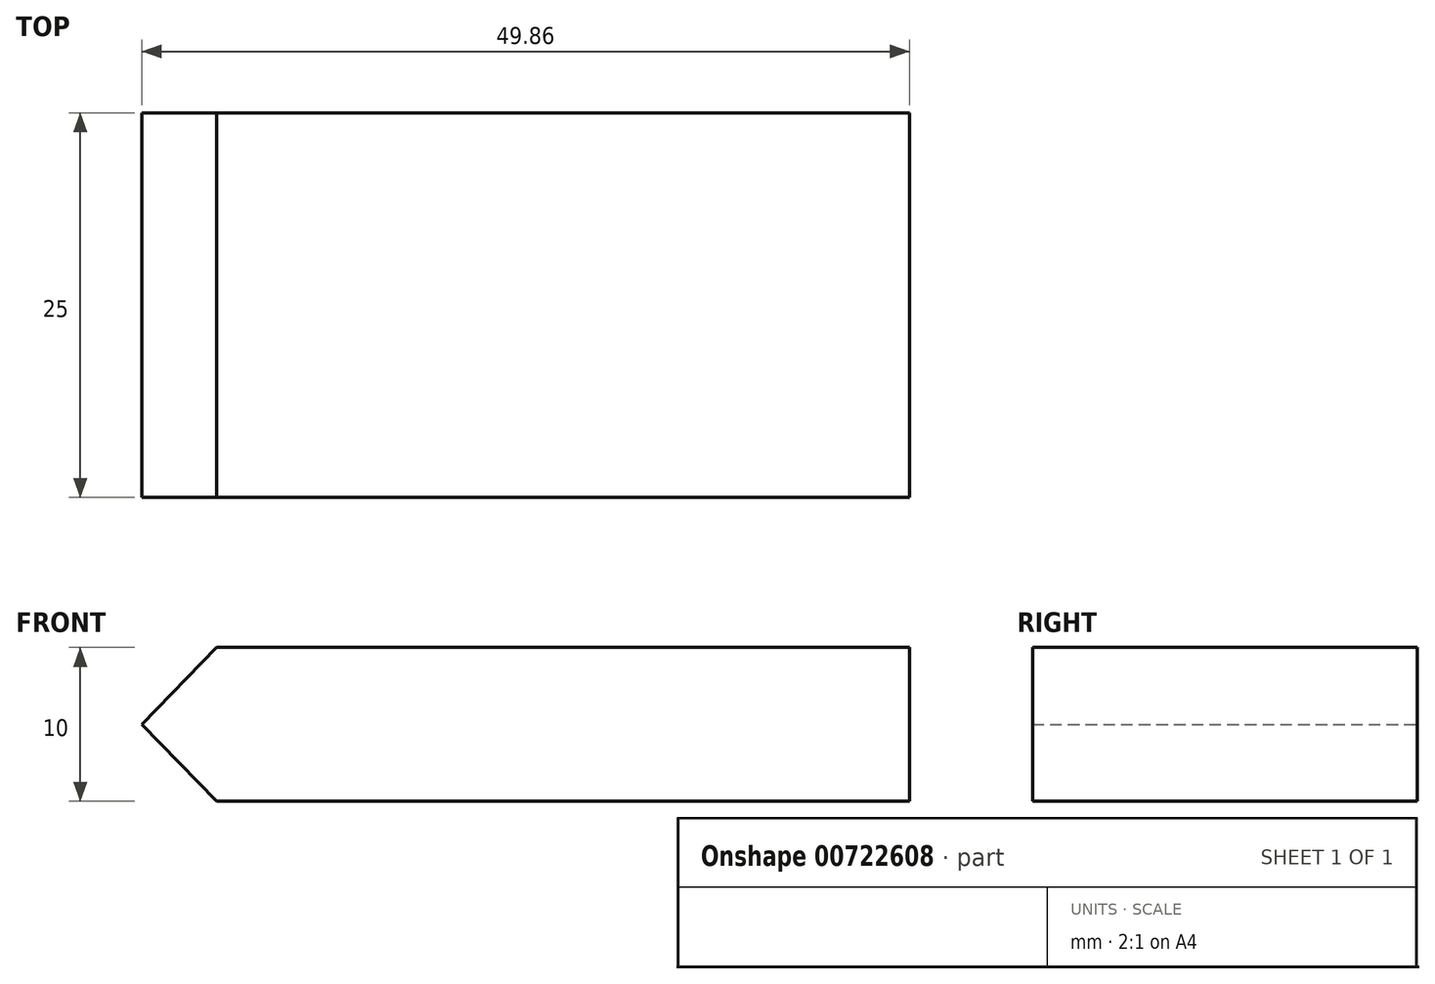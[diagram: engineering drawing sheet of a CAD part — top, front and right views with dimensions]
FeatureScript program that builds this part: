
annotation { "Feature Type Name" : "Feature", "Feature Type Description" : "" }
export const myFeature = defineFeature(function(context is Context, id is Id, definition is map)
    precondition{}
    {
        {
            var Q0;
            Q0=qCreatedBy(makeId("Front.planeOp"),FACE);
            var sketch = newSketch(context, id + "F0", { "sketchPlane" : qUnion([Q0])});
            skLineSegment(sketch, "E0", {"start": v(0, 0) * mm, "end": v(4.86, 5) * mm});
            skLineSegment(sketch, "E1", {"start": v(49.86, 5) * mm, "end": v(49.86, -5) * mm});
            skLineSegment(sketch, "E2", {"start": v(4.86, -5) * mm, "end": v(0, 0) * mm});
            skLineSegment(sketch, "E3", {"start": v(4.86, 5) * mm, "end": v(49.86, 5) * mm});
            skLineSegment(sketch, "E4", {"start": v(4.86, -5) * mm, "end": v(49.86, -5) * mm});
            skPoint(sketch, "E5", {"position": v(44.86, 0) * mm});
            skPoint(sketch, "E6", {"position": v(9.86, 0) * mm});
            skSolve(sketch);
        }
        {
            var Q0;
            Q0=makeQuery(id+"F0.imprint","IMPRINT",FACE,{"disambiguationData":[TD([[makeQuery(id+"F0.imprint","IMPRINT",EDGE,{"derivedFrom":sQuery(id+"F0.wireOp",EDGE,"E0")}),-1.0]])]});
            extrude(context, id + "F1", {"entities" : qUnion([Q0]), "depth" : 25 * mm, "offsetDistance" : 25 * mm});
        }
    });
